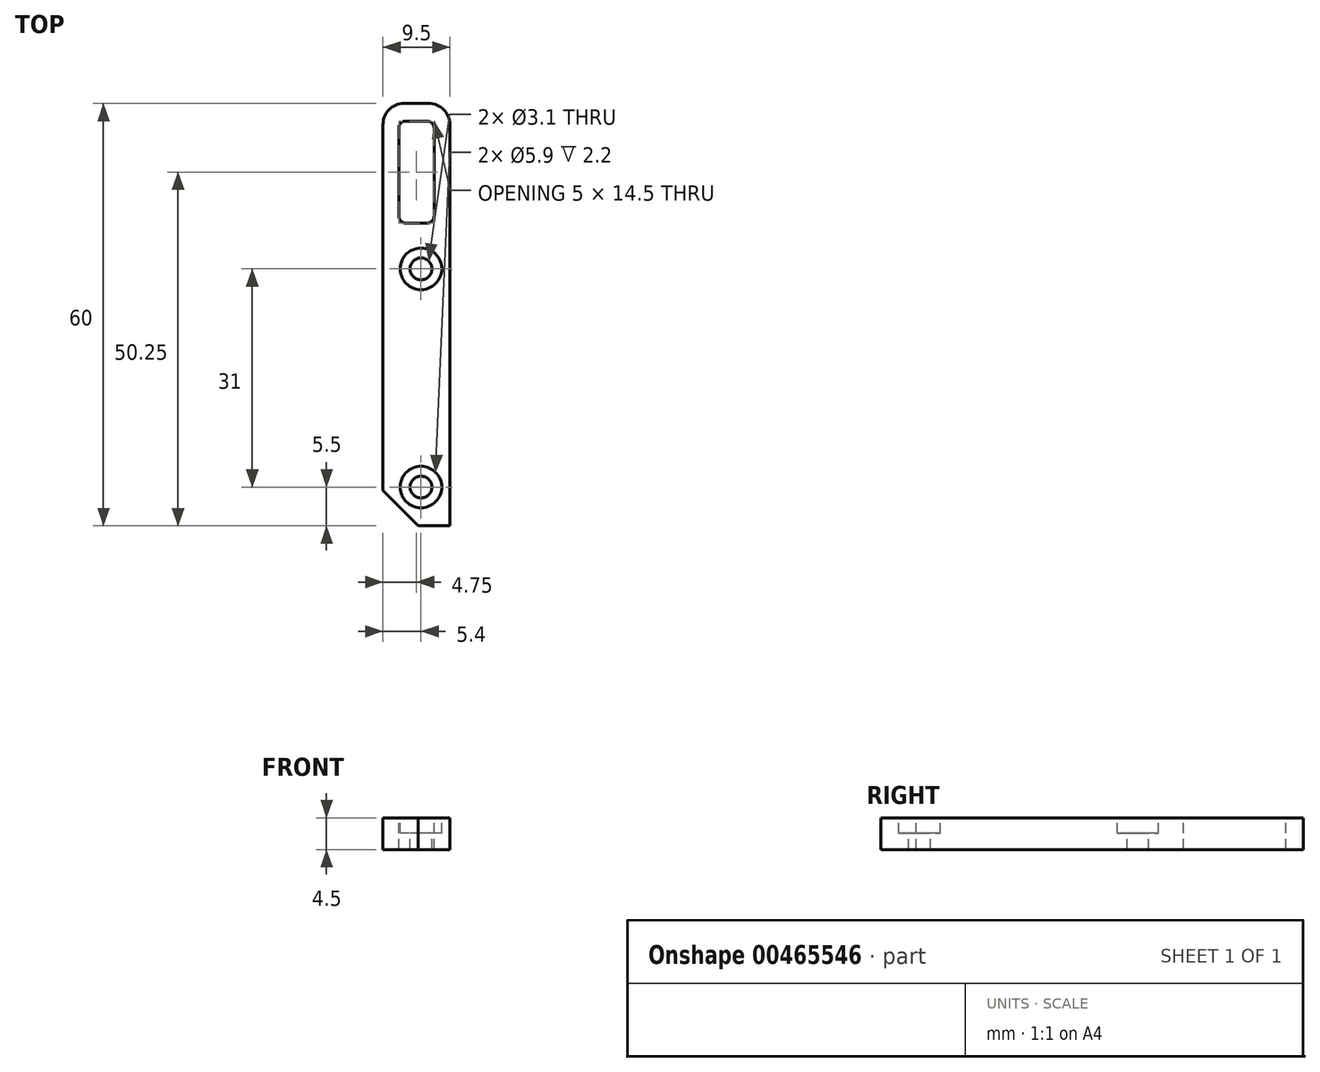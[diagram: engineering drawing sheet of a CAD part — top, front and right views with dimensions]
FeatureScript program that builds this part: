
annotation { "Feature Type Name" : "Feature", "Feature Type Description" : "" }
export const myFeature = defineFeature(function(context is Context, id is Id, definition is map)
    precondition{}
    {
        {
            var Q0;
            Q0=qCreatedBy(makeId("Top.planeOp"),FACE);
            var sketch = newSketch(context, id + "F0", { "sketchPlane" : qUnion([Q0])});
            skLineSegment(sketch, "E0.bottom", {"start": v(0, 0) * mm, "end": v(9.5, 0) * mm});
            skLineSegment(sketch, "E0.top", {"start": v(0, 60) * mm, "end": v(9.5, 60) * mm});
            skLineSegment(sketch, "E0.left", {"start": v(0, 0) * mm, "end": v(0, 60) * mm});
            skLineSegment(sketch, "E0.right", {"start": v(9.5, 0) * mm, "end": v(9.5, 60) * mm});
            skSolve(sketch);
        }
        {
            var Q0;
            Q0 = qSketchRegion(id + "F0", true);
            extrude(context, id + "F1", {"entities" : qUnion([Q0]), "depth" : 4.5 * mm});
        }
        {
            var Q0;
            Q0=makeQuery(id+"F1.opExtrude","CAP_FACE",FACE,{"disambiguationData":[OSD([sQuery(id+"F0.wireOp",EDGE,"E0.bottom"),sQuery(id+"F0.wireOp",EDGE,"E0.top"),sQuery(id+"F0.wireOp",EDGE,"E0.left"),sQuery(id+"F0.wireOp",EDGE,"E0.right")])],"isStart":false});
            var sketch = newSketch(context, id + "F2", { "sketchPlane" : qUnion([Q0])});
            skPoint(sketch, "E1", {"position": v(5.4, 5.5) * mm});
            skPoint(sketch, "E2", {"position": v(5.4, 36.5) * mm});
            skSolve(sketch);
        }
        {
            var Q0;
            Q0=makeQuery(id+"F1.opExtrude","CAP_FACE",FACE,{"disambiguationData":[OSD([sQuery(id+"F0.wireOp",EDGE,"E0.bottom"),sQuery(id+"F0.wireOp",EDGE,"E0.top"),sQuery(id+"F0.wireOp",EDGE,"E0.left"),sQuery(id+"F0.wireOp",EDGE,"E0.right")])],"isStart":false});
            var sketch = newSketch(context, id + "F3", { "sketchPlane" : qUnion([Q0])});
            skLineSegment(sketch, "E3.bottom", {"start": v(3.25, 57.5) * mm, "end": v(6.25, 57.5) * mm});
            skLineSegment(sketch, "E3.top", {"start": v(3.25, 43) * mm, "end": v(6.25, 43) * mm});
            skLineSegment(sketch, "E3.left", {"start": v(2.25, 56.5) * mm, "end": v(2.25, 44) * mm});
            skLineSegment(sketch, "E3.right", {"start": v(7.25, 56.5) * mm, "end": v(7.25, 44) * mm});
            skPoint(sketch, "E4.visualSharp", {"position": v(2.25, 57.5) * mm});
            skArc(sketch, "E4.filletArc", {"start": v(3.25, 57.5) * mm, "mid": v(2.54, 57.2) * mm, "end": v(2.25, 56.5) * mm});
            skPoint(sketch, "E5.visualSharp", {"position": v(7.25, 57.5) * mm});
            skArc(sketch, "E5.filletArc", {"start": v(7.25, 56.5) * mm, "mid": v(6.96, 57.2) * mm, "end": v(6.25, 57.5) * mm});
            skPoint(sketch, "E6.visualSharp", {"position": v(2.25, 43) * mm});
            skArc(sketch, "E6.filletArc", {"start": v(2.25, 44) * mm, "mid": v(2.54, 43.3) * mm, "end": v(3.25, 43) * mm});
            skPoint(sketch, "E7.visualSharp", {"position": v(7.25, 43) * mm});
            skArc(sketch, "E7.filletArc", {"start": v(6.25, 43) * mm, "mid": v(6.96, 43.3) * mm, "end": v(7.25, 44) * mm});
            skSolve(sketch);
        }
        {
            var Q0;
            Q0=sQuery(id+"F2.wireOp",VERTEX,"E2");
            var Q1;
            Q1=sQuery(id+"F2.wireOp",VERTEX,"E1");
            var Q2;
            Q2=makeQuery(id+"F1.opExtrude","SWEPT_BODY",BODY,{"disambiguationData":[OSD([sQuery(id+"F0.wireOp",EDGE,"E0.bottom"),sQuery(id+"F0.wireOp",EDGE,"E0.top"),sQuery(id+"F0.wireOp",EDGE,"E0.left"),sQuery(id+"F0.wireOp",EDGE,"E0.right")])]});
            hole(context, id + "F4", {"style" : HoleStyle.C_BORE, "endStyle" : HoleEndStyle.THROUGH, "holeDiameter" : 3.1 * mm, "cBoreDiameter" : 5.9 * mm, "cBoreDepth" : 2.2 * mm, "tappedDepth" : 12 * mm, "tapClearance" : 3, "locations" : qUnion([Q0, Q1]), "scope" : qUnion([Q2])});
        }
        {
            var Q0;
            Q0 = qSketchRegion(id + "F3", true);
            extrude(context, id + "F5", {"entities" : qUnion([Q0]), "operationType" : NewBodyOperationType.REMOVE, "oppositeDirection" : true, "depth" : 25 * mm});
        }
        {
            var Q0;
            Q0=makeQuery(id+"F1.opExtrude","SWEPT_EDGE",EDGE,{"disambiguationData":[OSD([sQuery(id+"F0.wireOp",EDGE,"E0.bottom"),sQuery(id+"F0.wireOp",EDGE,"E0.left")])]});
            chamfer(context, id + "F6", {"entities" : qUnion([Q0]), "width" : 5 * mm, "tangentPropagation" : true});
        }
        {
            var Q0;
            Q0=makeQuery(id+"F1.opExtrude","SWEPT_EDGE",EDGE,{"disambiguationData":[OSD([sQuery(id+"F0.wireOp",EDGE,"E0.top"),sQuery(id+"F0.wireOp",EDGE,"E0.left")])]});
            var Q1;
            Q1=makeQuery(id+"F1.opExtrude","SWEPT_EDGE",EDGE,{"disambiguationData":[OSD([sQuery(id+"F0.wireOp",EDGE,"E0.top"),sQuery(id+"F0.wireOp",EDGE,"E0.right")])]});
            fillet(context, id + "F7", {"entities" : qUnion([Q0, Q1]), "radius" : 3 * mm, "tangentPropagation" : true, "allowEdgeOverflow" : false});
        }
    });
